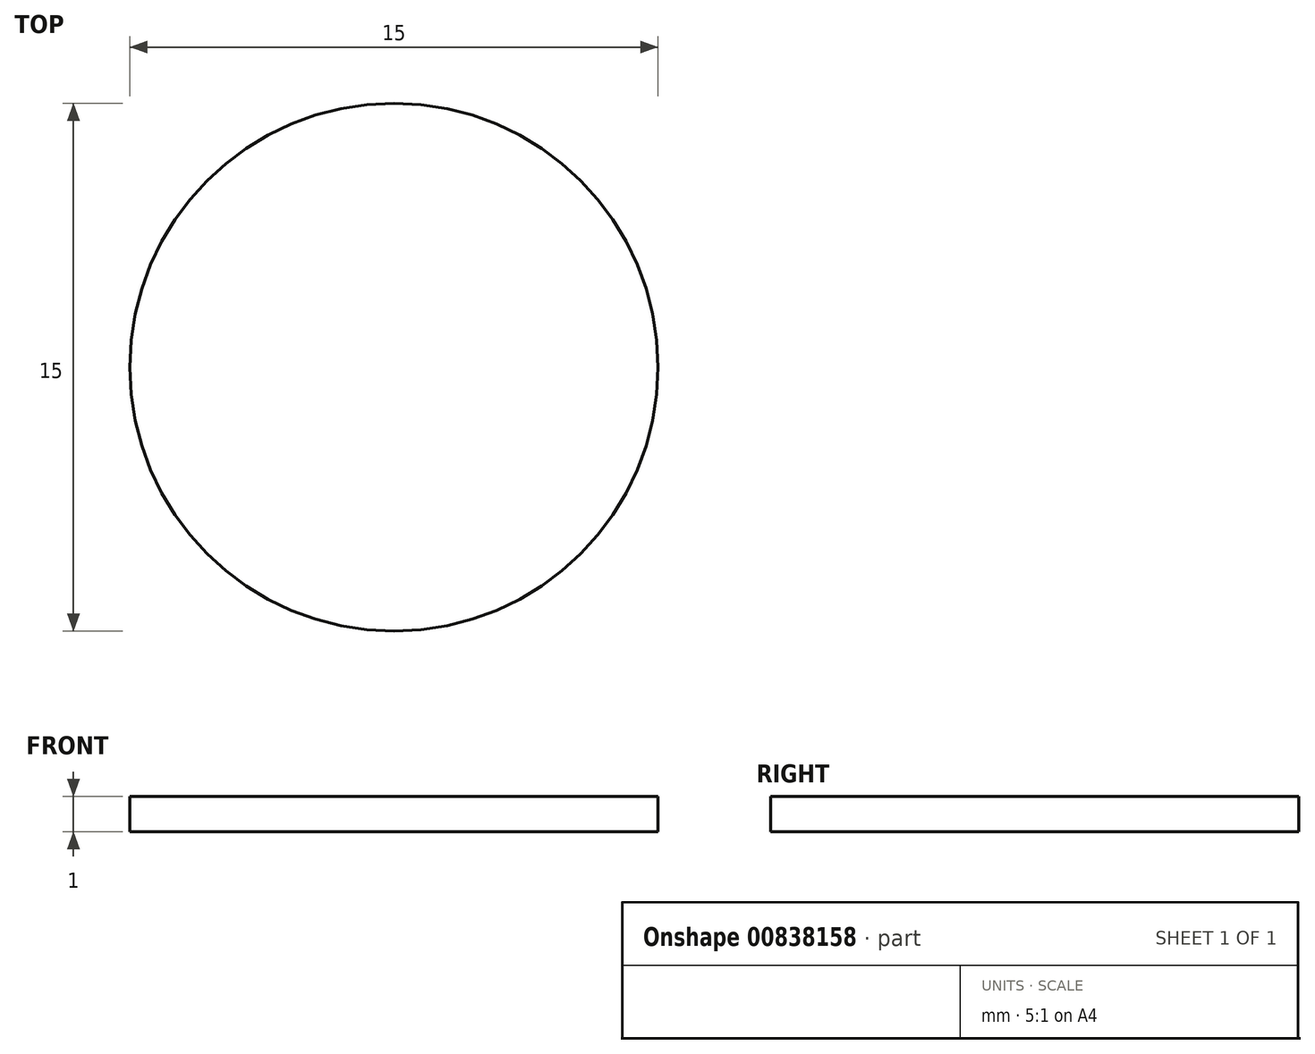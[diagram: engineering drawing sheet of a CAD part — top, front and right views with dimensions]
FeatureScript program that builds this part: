
annotation { "Feature Type Name" : "Feature", "Feature Type Description" : "" }
export const myFeature = defineFeature(function(context is Context, id is Id, definition is map)
    precondition{}
    {
        {
            var Q0;
            Q0=qCreatedBy(makeId("Top.planeOp"),FACE);
            var sketch = newSketch(context, id + "F0", { "sketchPlane" : qUnion([Q0])});
            skCircle(sketch, "E0", {"center": v(0, 0) * mm, "radius": 7.5 * mm});
            skSolve(sketch);
        }
        {
            var Q0;
            Q0=makeQuery(id+"F0.imprint","IMPRINT",FACE,{"disambiguationData":[TD([[makeQuery(id+"F0.imprint","IMPRINT",EDGE,{"derivedFrom":sQuery(id+"F0.wireOp",EDGE,"E0")}),1.0]])]});
            extrude(context, id + "F1", {"entities" : qUnion([Q0]), "depth" : 1 * mm, "offsetDistance" : 25 * mm});
        }
    });
